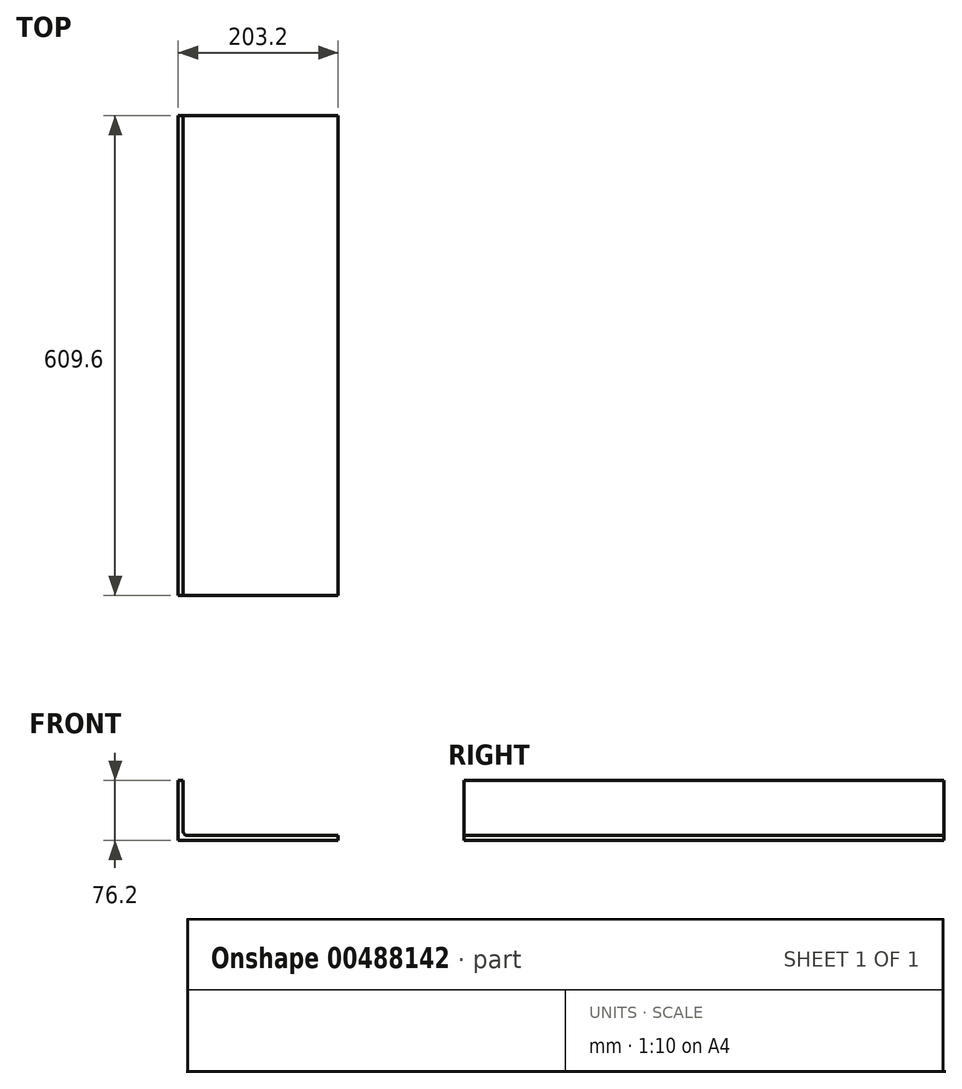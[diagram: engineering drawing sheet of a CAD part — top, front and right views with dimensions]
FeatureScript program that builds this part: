
annotation { "Feature Type Name" : "Feature", "Feature Type Description" : "" }
export const myFeature = defineFeature(function(context is Context, id is Id, definition is map)
    precondition{}
    {
        {
            var Q0;
            Q0=qCreatedBy(makeId("Front.planeOp"),FACE);
            var sketch = newSketch(context, id + "F0", { "sketchPlane" : qUnion([Q0])});
            skLineSegment(sketch, "E0", {"start": v(0, 0) * mm, "end": v(0, 76.2) * mm});
            skLineSegment(sketch, "E1", {"start": v(0, 0) * mm, "end": v(203.2, 0) * mm});
            skLineSegment(sketch, "E2", {"start": v(203.2, 0) * mm, "end": v(203.2, 6.35) * mm});
            skLineSegment(sketch, "E3", {"start": v(203.2, 6.35) * mm, "end": v(6.35, 6.35) * mm});
            skLineSegment(sketch, "E4", {"start": v(6.35, 6.35) * mm, "end": v(6.35, 76.2) * mm});
            skLineSegment(sketch, "E5", {"start": v(6.35, 76.2) * mm, "end": v(0, 76.2) * mm});
            skSolve(sketch);
        }
        {
            var Q0;
            Q0=makeQuery(id+"F0.imprint","IMPRINT",FACE,{"disambiguationData":[TD([[makeQuery(id+"F0.imprint","IMPRINT",EDGE,{"derivedFrom":sQuery(id+"F0.wireOp",EDGE,"E0")}),-1.0]])]});
            extrude(context, id + "F1", {"entities" : qUnion([Q0]), "oppositeDirection" : true, "depth" : 609.6 * mm, "offsetDistance" : 25.4 * mm});
        }
        {
            var Q0;
            Q0=makeQuery(id+"F1.opExtrude","SWEPT_EDGE",EDGE,{"disambiguationData":[OSD([sQuery(id+"F0.wireOp",EDGE,"E3"),sQuery(id+"F0.wireOp",EDGE,"E4")])]});
            fillet(context, id + "F2", {"entities" : qUnion([Q0]), "radius" : 5.08 * mm, "tangentPropagation" : true, "allowEdgeOverflow" : false});
        }
    });
